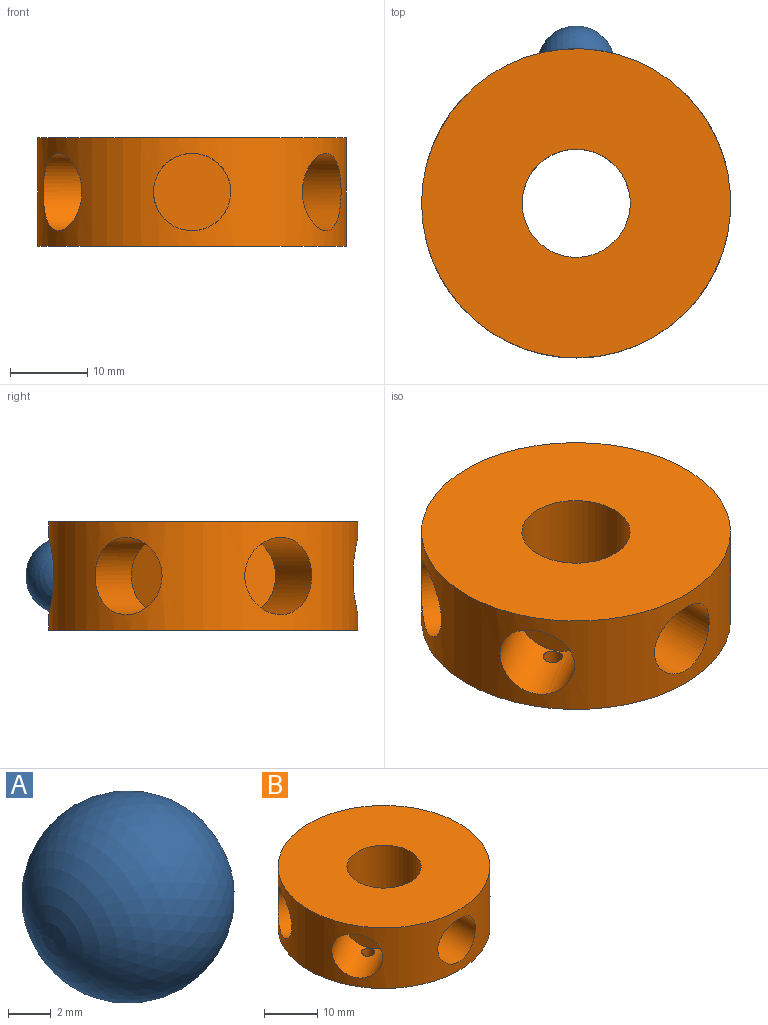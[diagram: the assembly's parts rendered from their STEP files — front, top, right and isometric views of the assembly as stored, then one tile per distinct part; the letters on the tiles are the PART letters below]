
ASSEMBLY  parts=2 mates=1
PART A: 1 faces, bbox 10x10x10 mm
  f0: sphere r=5mm, area 314.2mm2
PART B: 22 faces, bbox 40x40x14 mm
  f0: cylinder r=7mm len=14mm, axis (0,0,-1), area 615.8mm2, adj f2,f3
  f1: cylinder r=20mm len=40mm, axis (0,0,-1), area 1283.5mm2, adj f2,f3,f4,f6,f8,f10,f12,f14
  f2: plane 40x40mm, normal (0,0,1), area 1102.7mm2, adj f0,f1
  f3: plane 40x40mm, normal (0,0,-1), area 1073.2mm2, adj f0,f1,f16,f17,f18,f19,f20,f21
  f4: cylinder r=5mm len=10mm, axis (0,-1,0), area 299.3mm2, adj f1,f5,f21
  f5: plane 10x10mm, normal (0,-1,0), area 78.5mm2, adj f4
  f6: cylinder r=5mm len=10mm, axis (0,1,0), area 299.3mm2, adj f1,f7,f20
  f7: plane 10x10mm, normal (0,1,0), area 78.5mm2, adj f6
  f8: cylinder r=5mm len=13.66mm, axis (0.87,0.5,0), area 299.3mm2, adj f1,f9,f19
  f9: plane 10x8.66mm, normal (0.87,0.5,0), area 78.5mm2, adj f8
  f10: cylinder r=5mm len=13.66mm, axis (0.87,-0.5,0), area 299.3mm2, adj f1,f11,f18
  f11: plane 10x8.66mm, normal (0.87,-0.5,0), area 78.5mm2, adj f10
  f12: cylinder r=5mm len=13.66mm, axis (-0.87,0.5,0), area 299.3mm2, adj f1,f13,f17
  f13: plane 10x8.66mm, normal (-0.87,0.5,0), area 78.5mm2, adj f12
  f14: cylinder r=5mm len=13.66mm, axis (-0.87,-0.5,0), area 299.3mm2, adj f1,f15,f16
  f15: plane 10x8.66mm, normal (-0.87,-0.5,0), area 78.5mm2, adj f14
  f16: cylinder r=1.25mm len=2.5mm, axis (0,0,-1), area 16.3mm2, adj f3,f14
  f17: cylinder r=1.25mm len=2.5mm, axis (0,0,-1), area 16.3mm2, adj f3,f12
  f18: cylinder r=1.25mm len=2.5mm, axis (0,0,-1), area 16.3mm2, adj f3,f10
  f19: cylinder r=1.25mm len=2.5mm, axis (0,0,-1), area 16.3mm2, adj f3,f8
  f20: cylinder r=1.25mm len=2.5mm, axis (0,0,-1), area 16.3mm2, adj f3,f6
  f21: cylinder r=1.25mm len=2.5mm, axis (0,0,-1), area 16.3mm2, adj f3,f4
PLACE A rot(axis=(-1,0,0),90deg) t=(-5.45,20.07,7.08)mm
PLACE B rot(axis=(0,0,1),60deg) t=(-0.45,2.1,0.08)mm
MATE cylindrical B.f8 <-> A.f0  axis (0,1,0) through (-0.45,17.13,7.08)mm
